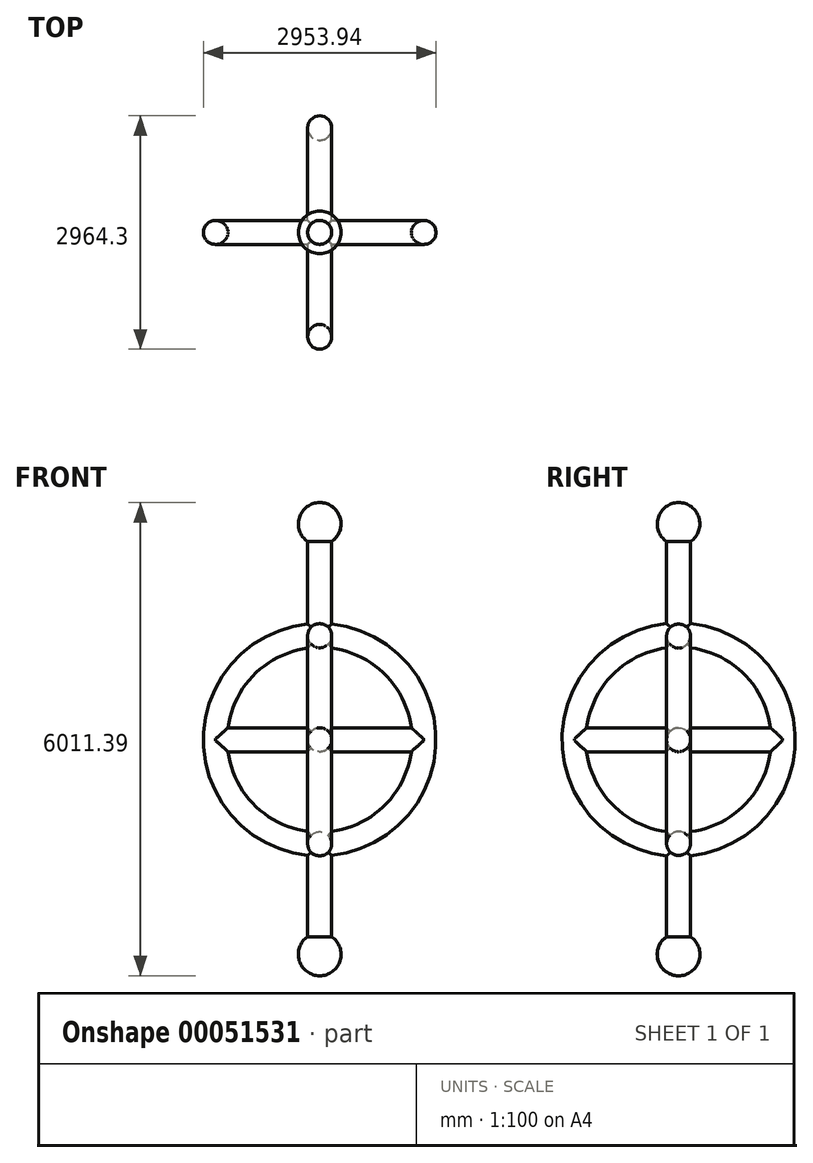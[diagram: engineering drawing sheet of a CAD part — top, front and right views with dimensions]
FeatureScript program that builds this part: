
annotation { "Feature Type Name" : "Feature", "Feature Type Description" : "" }
export const myFeature = defineFeature(function(context is Context, id is Id, definition is map)
    precondition{}
    {
        {
            var Q0;
            Q0=qCreatedBy(makeId("Right.planeOp"),FACE);
            var sketch = newSketch(context, id + "F0", { "sketchPlane" : qUnion([Q0])});
            skCircle(sketch, "E0", {"center": v(0, 0) * mm, "radius": 152.4 * mm});
            skSolve(sketch);
        }
        {
            var Q0;
            Q0=makeQuery(id+"F0.imprint","IMPRINT",FACE,{"disambiguationData":[TD([[makeQuery(id+"F0.imprint","IMPRINT",EDGE,{"derivedFrom":sQuery(id+"F0.wireOp",EDGE,"E0")}),1.0]])]});
            extrude(context, id + "F1", {"entities" : qUnion([Q0]), "depth" : 1320.8 * mm, "hasSecondDirection" : true, "secondDirectionOppositeDirection" : true, "secondDirectionDepth" : 1320.8 * mm});
        }
        {
            var Q0;
            Q0=qCreatedBy(makeId("Top.planeOp"),FACE);
            var sketch = newSketch(context, id + "F2", { "sketchPlane" : qUnion([Q0])});
            skCircle(sketch, "E1", {"center": v(1325.17, 0) * mm, "radius": 151.8 * mm});
            skLineSegment(sketch, "E2", {"start": v(0, 647.9) * mm, "end": v(0, -365.34) * mm});
            skSolve(sketch);
        }
        {
            var Q0;
            Q0 = qSketchRegion(id + "F2", true);
            var Q1;
            Q1=sQuery(id+"F2.wireOp",EDGE,"E2");
            revolve(context, id + "F3", {"operationType" : NewBodyOperationType.ADD, "entities" : qUnion([Q0]), "axis" : qUnion([Q1]), "revolveType" : RevolveType.FULL});
        }
        {
            var Q0;
            Q0=qCreatedBy(makeId("Front.planeOp"),FACE);
            var sketch = newSketch(context, id + "F4", { "sketchPlane" : qUnion([Q0])});
            skCircle(sketch, "E3", {"center": v(0, 0) * mm, "radius": 152.4 * mm});
            skSolve(sketch);
        }
        {
            var Q0;
            Q0 = qSketchRegion(id + "F4", true);
            extrude(context, id + "F5", {"entities" : qUnion([Q0]), "operationType" : NewBodyOperationType.ADD, "depth" : 1320.8 * mm, "hasSecondDirection" : true, "secondDirectionOppositeDirection" : true, "secondDirectionDepth" : 1320.8 * mm});
        }
        {
            var Q0;
            Q0=qCreatedBy(makeId("Top.planeOp"),FACE);
            var sketch = newSketch(context, id + "F6", { "sketchPlane" : qUnion([Q0])});
            skCircle(sketch, "E4", {"center": v(0, -1329.75) * mm, "radius": 152.4 * mm});
            skLineSegment(sketch, "E5", {"start": v(-1356.82, 0) * mm, "end": v(1763.06, 0) * mm});
            skSolve(sketch);
        }
        {
            var Q0;
            Q0 = qSketchRegion(id + "F6", true);
            var Q1;
            Q1=sQuery(id+"F6.wireOp",EDGE,"E5");
            revolve(context, id + "F7", {"operationType" : NewBodyOperationType.ADD, "entities" : qUnion([Q0]), "axis" : qUnion([Q1]), "revolveType" : RevolveType.FULL});
        }
        {
            var Q0;
            Q0=qCreatedBy(makeId("Top.planeOp"),FACE);
            var sketch = newSketch(context, id + "F8", { "sketchPlane" : qUnion([Q0])});
            skCircle(sketch, "E6", {"center": v(0, 0) * mm, "radius": 152.4 * mm});
            skSolve(sketch);
        }
        {
            var Q0;
            Q0 = qSketchRegion(id + "F8", true);
            extrude(context, id + "F9", {"entities" : qUnion([Q0]), "operationType" : NewBodyOperationType.ADD, "depth" : 25.4 * mm});
        }
        {
            var Q0;
            Q0=qCreatedBy(makeId("Top.planeOp"),FACE);
            var sketch = newSketch(context, id + "F10", { "sketchPlane" : qUnion([Q0])});
            skCircle(sketch, "E7", {"center": v(0, 0) * mm, "radius": 152.4 * mm});
            skSolve(sketch);
        }
        {
            var Q0;
            Q0 = qSketchRegion(id + "F10", true);
            extrude(context, id + "F11", {"entities" : qUnion([Q0]), "operationType" : NewBodyOperationType.ADD, "depth" : 2743.2 * mm, "hasSecondDirection" : true, "secondDirectionOppositeDirection" : true, "secondDirectionDepth" : 2743.2 * mm});
        }
        {
            var Q0;
            Q0=qCreatedBy(makeId("Front.planeOp"),FACE);
            var sketch = newSketch(context, id + "F12", { "sketchPlane" : qUnion([Q0])});
            skArc(sketch, "E8", {"start": v(0, 2471.33) * mm, "mid": v(270.75, 2742.08) * mm, "end": v(0, 3012.83) * mm});
            skLineSegment(sketch, "E9", {"start": v(0, 3012.83) * mm, "end": v(0, 2471.33) * mm});
            skSolve(sketch);
        }
        {
            var Q0;
            Q0 = qSketchRegion(id + "F12", true);
            var Q1;
            Q1=sQuery(id+"F12.wireOp",EDGE,"E9");
            revolve(context, id + "F13", {"operationType" : NewBodyOperationType.ADD, "entities" : qUnion([Q0]), "axis" : qUnion([Q1]), "revolveType" : RevolveType.FULL});
        }
        {
            var Q0;
            Q0=qCreatedBy(makeId("Right.planeOp"),FACE);
            var sketch = newSketch(context, id + "F14", { "sketchPlane" : qUnion([Q0])});
            skArc(sketch, "E10", {"start": v(0, -2455.25) * mm, "mid": v(-271.65, -2726.9) * mm, "end": v(0, -2998.56) * mm});
            skLineSegment(sketch, "E11", {"start": v(0, -2455.25) * mm, "end": v(0, -2998.56) * mm});
            skSolve(sketch);
        }
        {
            var Q0;
            Q0 = qSketchRegion(id + "F14", true);
            var Q1;
            Q1=sQuery(id+"F14.wireOp",EDGE,"E11");
            revolve(context, id + "F15", {"operationType" : NewBodyOperationType.ADD, "entities" : qUnion([Q0]), "axis" : qUnion([Q1]), "revolveType" : RevolveType.FULL});
        }
    });
